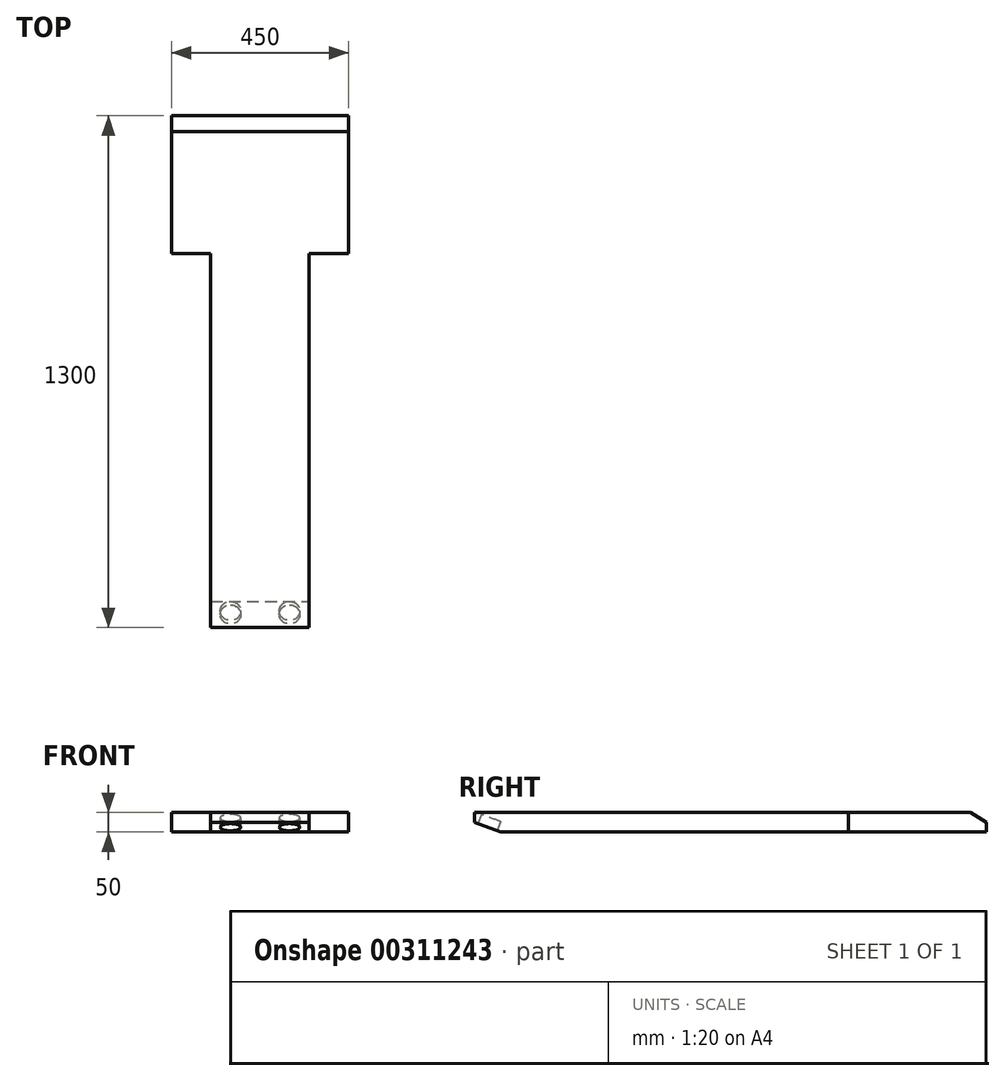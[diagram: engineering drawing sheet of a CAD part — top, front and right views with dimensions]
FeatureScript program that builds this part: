
annotation { "Feature Type Name" : "Feature", "Feature Type Description" : "" }
export const myFeature = defineFeature(function(context is Context, id is Id, definition is map)
    precondition{}
    {
        {
            var Q0;
            Q0=qCreatedBy(makeId("Top.planeOp"),FACE);
            var sketch = newSketch(context, id + "F0", { "sketchPlane" : qUnion([Q0])});
            skLineSegment(sketch, "E0.bottom", {"start": v(-440.03, 1254.35) * mm, "end": v(9.97, 1254.35) * mm});
            skLineSegment(sketch, "E0.top", {"start": v(-440.03, -45.65) * mm, "end": v(9.97, -45.65) * mm});
            skLineSegment(sketch, "E0.left", {"start": v(-440.03, 1254.35) * mm, "end": v(-440.03, -45.65) * mm});
            skLineSegment(sketch, "E0.right", {"start": v(9.97, 1254.35) * mm, "end": v(9.97, -45.65) * mm});
            skSolve(sketch);
        }
        {
            var Q0;
            Q0=makeQuery(id+"F0.imprint","IMPRINT",FACE,{"disambiguationData":[TD([[makeQuery(id+"F0.imprint","IMPRINT",EDGE,{"derivedFrom":sQuery(id+"F0.wireOp",EDGE,"E0.bottom")}),-1.0]])]});
            extrude(context, id + "F1", {"entities" : qUnion([Q0]), "depth" : 50 * mm});
        }
        {
            var Q0;
            Q0=makeQuery(id+"F1.opExtrude","CAP_FACE",FACE,{"disambiguationData":[OSD([sQuery(id+"F0.wireOp",EDGE,"E0.bottom"),sQuery(id+"F0.wireOp",EDGE,"E0.top"),sQuery(id+"F0.wireOp",EDGE,"E0.left"),sQuery(id+"F0.wireOp",EDGE,"E0.right")])],"isStart":false});
            var sketch = newSketch(context, id + "F2", { "sketchPlane" : qUnion([Q0])});
            skLineSegment(sketch, "E1", {"start": v(-440.03, 1254.35) * mm, "end": v(-440.03, 904.35) * mm});
            skLineSegment(sketch, "E2", {"start": v(-440.03, 904.35) * mm, "end": v(-340.03, 904.35) * mm});
            skLineSegment(sketch, "E3", {"start": v(-340.03, 904.35) * mm, "end": v(-340.03, -45.65) * mm});
            skLineSegment(sketch, "E4", {"start": v(-340.03, -45.65) * mm, "end": v(-90.03, -45.65) * mm});
            skLineSegment(sketch, "E5", {"start": v(-90.03, -45.65) * mm, "end": v(-90.03, 904.35) * mm});
            skLineSegment(sketch, "E6", {"start": v(-90.03, 904.35) * mm, "end": v(9.97, 904.35) * mm});
            skLineSegment(sketch, "E7", {"start": v(9.97, 904.35) * mm, "end": v(9.97, 1254.35) * mm});
            skLineSegment(sketch, "E8", {"start": v(9.97, 1254.35) * mm, "end": v(-440.03, 1254.35) * mm});
            skSolve(sketch);
        }
        {
            var Q0;
            {var subQ0=sQuery(id+"F2.wireOp",EDGE,"E2");Q0=makeQuery(id+"F2.imprint","IMPRINT",FACE,{"disambiguationData":[TD([[makeQuery(id+"F2.imprint","IMPRINT",EDGE,{"derivedFrom":subQ0}),-1.0]])]});}
            var Q1;
            {var subQ0=sQuery(id+"F2.wireOp",EDGE,"E5");Q1=makeQuery(id+"F2.imprint","IMPRINT",FACE,{"disambiguationData":[TD([[makeQuery(id+"F2.imprint","IMPRINT",EDGE,{"derivedFrom":subQ0}),-1.0]])]});}
            extrude(context, id + "F3", {"entities" : qUnion([Q0, Q1]), "operationType" : NewBodyOperationType.REMOVE, "endBound" : BoundingType.THROUGH_ALL, "oppositeDirection" : true, "depth" : 25.4 * mm});
        }
        {
            var Q0;
            Q0=makeQuery(id+"F3.boolean.opBoolean","COPY",FACE,{"derivedFrom":makeQuery(id+"F3.opExtrude","SWEPT_FACE",FACE,{"disambiguationData":[OSD([sQuery(id+"F2.wireOp",EDGE,"E5")])]})});
            var sketch = newSketch(context, id + "F4", { "sketchPlane" : qUnion([Q0])});
            skLineSegment(sketch, "E9", {"start": v(-45.65, 25) * mm, "end": v(20.68, 0) * mm});
            skSolve(sketch);
        }
        {
            var Q0;
            {var subQ0=sQuery(id+"F4.wireOp",EDGE,"E9");Q0=makeQuery(id+"F4.imprint","IMPRINT",FACE,{"disambiguationData":[TD([[makeQuery(id+"F4.imprint","IMPRINT",EDGE,{"derivedFrom":subQ0}),-1.0]])]});}
            extrude(context, id + "F5", {"entities" : qUnion([Q0]), "operationType" : NewBodyOperationType.REMOVE, "endBound" : BoundingType.THROUGH_ALL, "oppositeDirection" : true, "depth" : 25 * mm});
        }
        {
            var Q0;
            Q0=makeQuery(id+"F1.opExtrude","SWEPT_FACE",FACE,{"disambiguationData":[OSD([sQuery(id+"F0.wireOp",EDGE,"E0.right")])]});
            var sketch = newSketch(context, id + "F6", { "sketchPlane" : qUnion([Q0])});
            skLineSegment(sketch, "E10", {"start": v(1254.35, 25) * mm, "end": v(1214.1, 50) * mm});
            skLineSegment(sketch, "E11", {"start": v(1214.1, 50) * mm, "end": v(1254.35, 50) * mm});
            skLineSegment(sketch, "E12", {"start": v(1254.35, 50) * mm, "end": v(1254.35, 25) * mm});
            skSolve(sketch);
        }
        {
            var Q0;
            Q0=makeQuery(id+"F6.imprint","IMPRINT",FACE,{"disambiguationData":[TD([[makeQuery(id+"F6.imprint","IMPRINT",EDGE,{"derivedFrom":sQuery(id+"F6.wireOp",EDGE,"E10")}),-1.0]])]});
            extrude(context, id + "F7", {"entities" : qUnion([Q0]), "operationType" : NewBodyOperationType.REMOVE, "endBound" : BoundingType.THROUGH_ALL, "oppositeDirection" : true, "depth" : 25 * mm});
        }
        {
            var Q0;
            Q0=makeQuery(id+"F5.boolean.opBoolean","COPY",FACE,{"derivedFrom":makeQuery(id+"F5.opExtrude","SWEPT_FACE",FACE,{"disambiguationData":[OSD([sQuery(id+"F4.wireOp",EDGE,"E9")])]})});
            var sketch = newSketch(context, id + "F8", { "sketchPlane" : qUnion([Q0])});
            skCircle(sketch, "E13", {"center": v(-140.03, 16.1) * mm, "radius": 26 * mm});
            skCircle(sketch, "E14", {"center": v(-290.03, 16.1) * mm, "radius": 26 * mm});
            skSolve(sketch);
        }
        {
            var Q0;
            Q0 = qSketchRegion(id + "F8", true);
            extrude(context, id + "F9", {"entities" : qUnion([Q0]), "operationType" : NewBodyOperationType.REMOVE, "oppositeDirection" : true, "depth" : 25 * mm});
        }
    });
